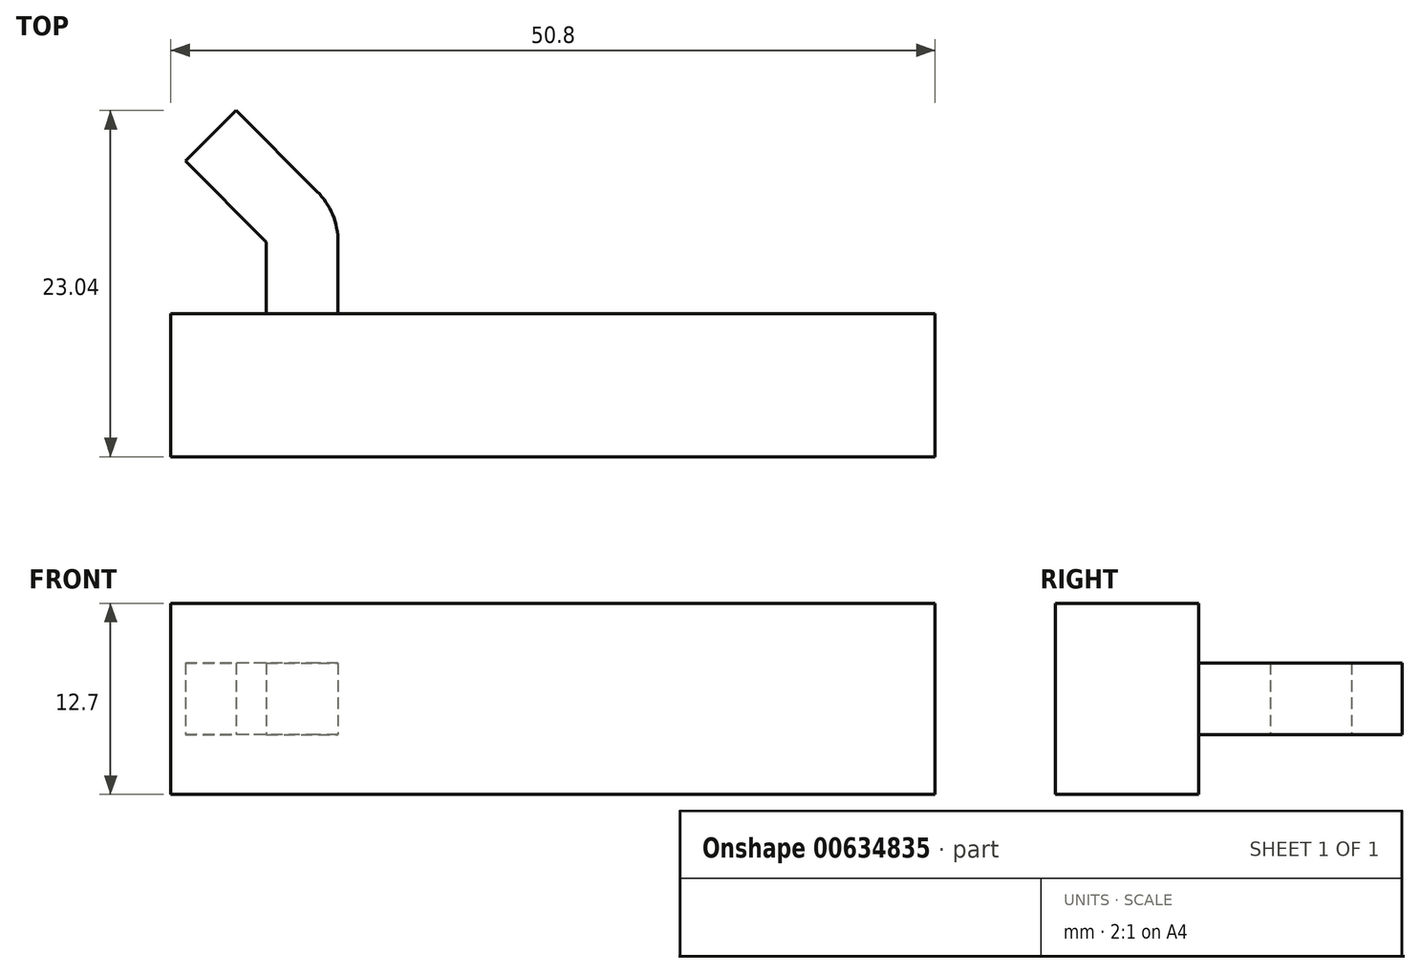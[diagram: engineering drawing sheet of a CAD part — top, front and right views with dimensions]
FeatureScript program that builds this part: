
annotation { "Feature Type Name" : "Feature", "Feature Type Description" : "" }
export const myFeature = defineFeature(function(context is Context, id is Id, definition is map)
    precondition{}
    {
        {
            var Q0;
            Q0=qCreatedBy(makeId("Top.planeOp"),FACE);
            var sketch = newSketch(context, id + "F0", { "sketchPlane" : qUnion([Q0])});
            skLineSegment(sketch, "E0.bottom", {"start": v(-4.76, -15.21) * mm, "end": v(0, -15.21) * mm});
            skLineSegment(sketch, "E0.top", {"start": v(-4.76, -10.45) * mm, "end": v(0, -10.45) * mm});
            skLineSegment(sketch, "E0.left", {"start": v(-4.76, -15.21) * mm, "end": v(-4.76, -10.45) * mm});
            skLineSegment(sketch, "E0.right", {"start": v(0, -15.21) * mm, "end": v(0, -10.45) * mm});
            skLineSegment(sketch, "E1", {"start": v(-4.76, -10.45) * mm, "end": v(-4.76, -5.07) * mm, "construction": true});
            skLineSegment(sketch, "E2", {"start": v(-4.76, -10.45) * mm, "end": v(-10.15, -5.07) * mm});
            skLineSegment(sketch, "E3", {"start": v(-10.15, -5.07) * mm, "end": v(-6.78, -1.7) * mm});
            skLineSegment(sketch, "E4", {"start": v(-4.76, -10.45) * mm, "end": v(-1.4, -7.08) * mm});
            skLineSegment(sketch, "E5", {"start": v(-1.4, -7.08) * mm, "end": v(-6.78, -1.7) * mm});
            skArc(sketch, "E6", {"start": v(-1.4, -7.08) * mm, "mid": v(-0.36, -8.63) * mm, "end": v(0, -10.45) * mm});
            skLineSegment(sketch, "E7.bottom", {"start": v(-11.11, -15.21) * mm, "end": v(39.69, -15.21) * mm});
            skLineSegment(sketch, "E7.top", {"start": v(-11.11, -24.74) * mm, "end": v(39.69, -24.74) * mm});
            skLineSegment(sketch, "E7.left", {"start": v(-11.11, -15.21) * mm, "end": v(-11.11, -24.74) * mm});
            skLineSegment(sketch, "E7.right", {"start": v(39.69, -15.21) * mm, "end": v(39.69, -24.74) * mm});
            skLineSegment(sketch, "E8", {"start": v(-4.76, -15.21) * mm, "end": v(-11.11, -15.21) * mm});
            skSolve(sketch);
        }
        {
            var Q0;
            Q0=makeQuery(id+"F0.imprint","IMPRINT",FACE,{"disambiguationData":[TD([[makeQuery(id+"F0.imprint","IMPRINT",EDGE,{"derivedFrom":sQuery(id+"F0.wireOp",EDGE,"E7.top")}),1.0]])]});
            extrude(context, id + "F1", {"entities" : qUnion([Q0]), "endBound" : BoundingType.SYMMETRIC, "depth" : 12.7 * mm, "offsetDistance" : 25.4 * mm});
        }
        {
            var Q0;
            Q0=makeQuery(id+"F0.imprint","IMPRINT",FACE,{"disambiguationData":[TD([[makeQuery(id+"F0.imprint","IMPRINT",EDGE,{"derivedFrom":sQuery(id+"F0.wireOp",EDGE,"E0.top")}),-1.0]])]});
            var Q1;
            Q1=makeQuery(id+"F0.imprint","IMPRINT",FACE,{"disambiguationData":[TD([[makeQuery(id+"F0.imprint","IMPRINT",EDGE,{"derivedFrom":sQuery(id+"F0.wireOp",EDGE,"E0.top")}),1.0]])]});
            var Q2;
            Q2=makeQuery(id+"F0.imprint","IMPRINT",FACE,{"disambiguationData":[TD([[makeQuery(id+"F0.imprint","IMPRINT",EDGE,{"derivedFrom":sQuery(id+"F0.wireOp",EDGE,"E2")}),-1.0]])]});
            extrude(context, id + "F2", {"entities" : qUnion([Q0, Q1, Q2]), "operationType" : NewBodyOperationType.ADD, "endBound" : BoundingType.SYMMETRIC, "depth" : 4.76 * mm, "offsetDistance" : 25.4 * mm});
        }
    });
